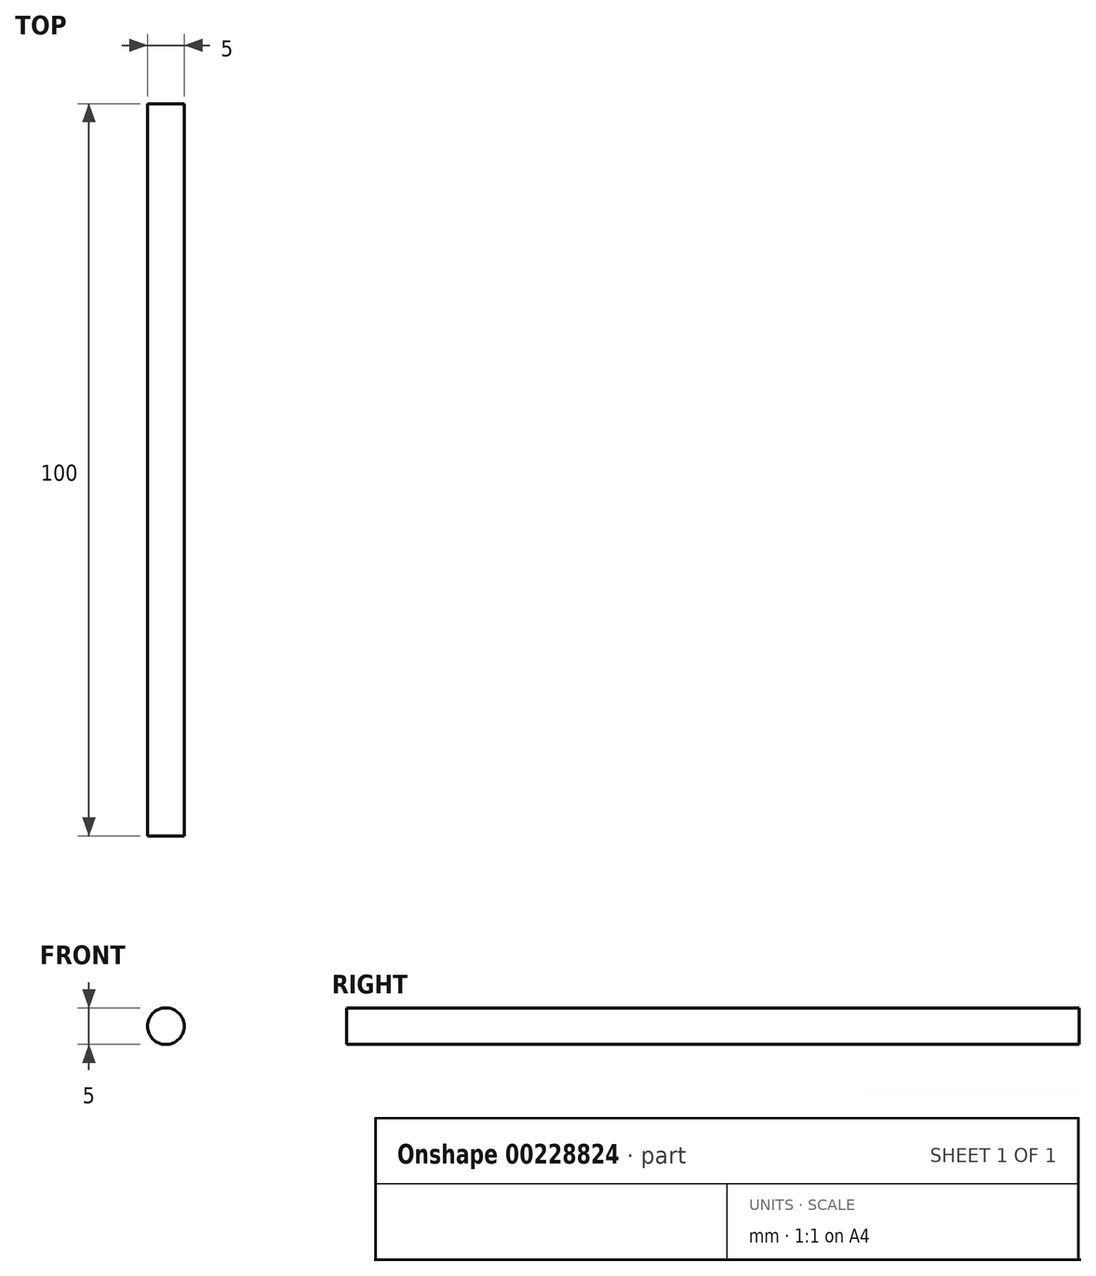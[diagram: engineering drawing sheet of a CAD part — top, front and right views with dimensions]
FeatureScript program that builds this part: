
annotation { "Feature Type Name" : "Feature", "Feature Type Description" : "" }
export const myFeature = defineFeature(function(context is Context, id is Id, definition is map)
    precondition{}
    {
        {
            var Q0;
            Q0=qCreatedBy(makeId("Front.planeOp"),FACE);
            var sketch = newSketch(context, id + "F0", { "sketchPlane" : qUnion([Q0])});
            skCircle(sketch, "E0", {"center": v(0, 0) * mm, "radius": 2.5 * mm});
            skSolve(sketch);
        }
        {
            var Q0;
            Q0=makeQuery(id+"F0.imprint","IMPRINT",FACE,{"disambiguationData":[TD([[makeQuery(id+"F0.imprint","IMPRINT",EDGE,{"derivedFrom":sQuery(id+"F0.wireOp",EDGE,"E0")}),1.0]])]});
            extrude(context, id + "F1", {"entities" : qUnion([Q0]), "depth" : 50 * mm, "hasSecondDirection" : true, "secondDirectionOppositeDirection" : true, "secondDirectionDepth" : 50 * mm});
        }
    });
